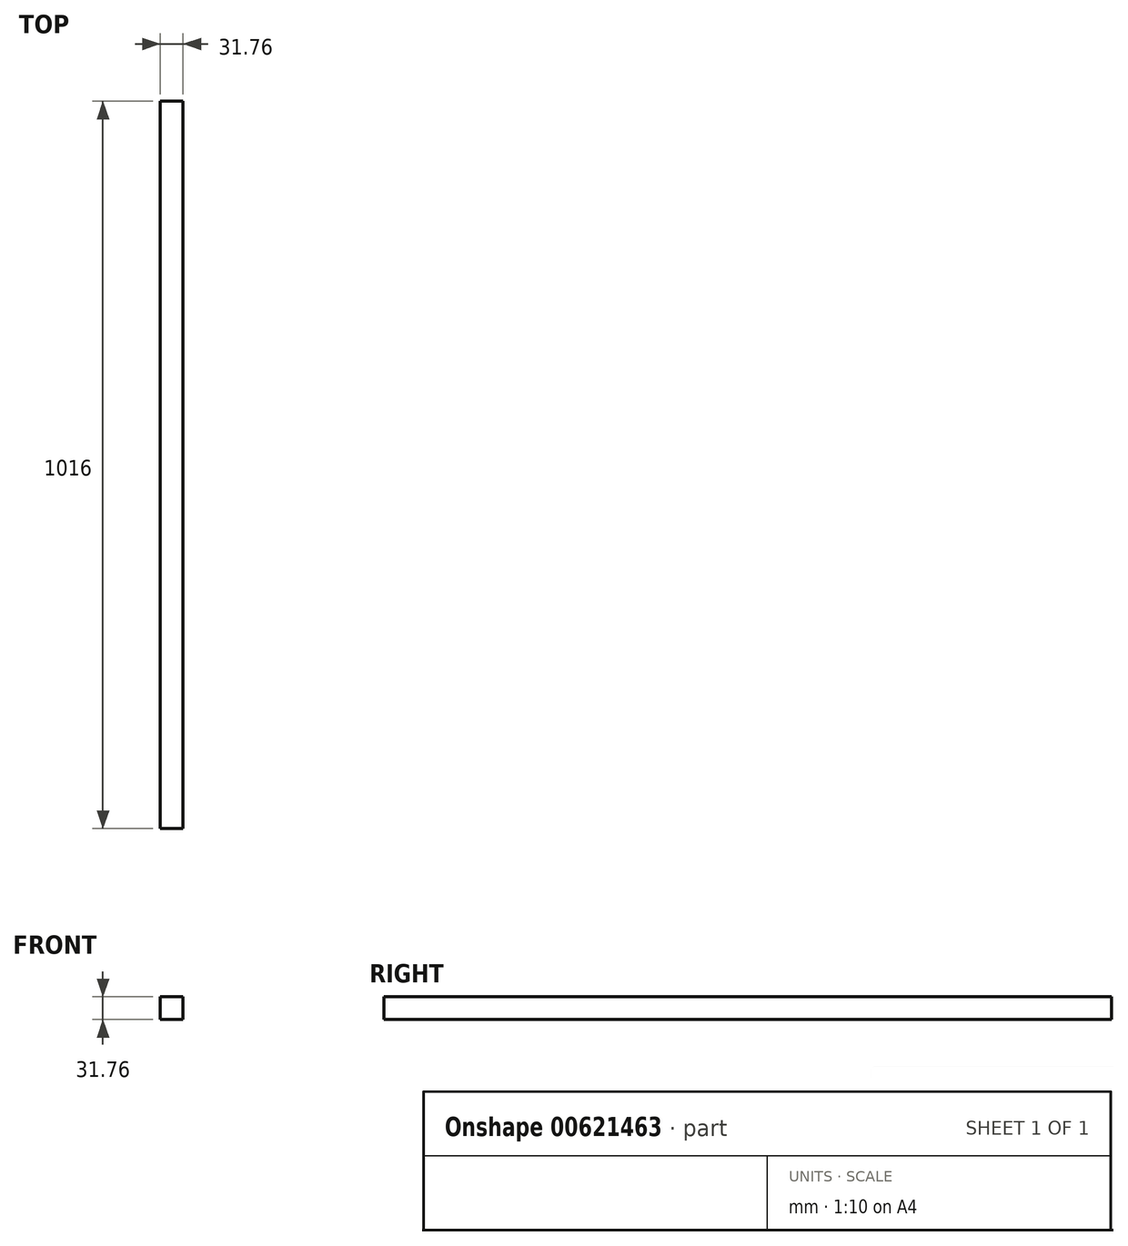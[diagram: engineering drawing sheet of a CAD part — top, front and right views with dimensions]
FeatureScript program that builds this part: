
annotation { "Feature Type Name" : "Feature", "Feature Type Description" : "" }
export const myFeature = defineFeature(function(context is Context, id is Id, definition is map)
    precondition{}
    {
        {
            var Q0;
            Q0=qCreatedBy(makeId("Front.planeOp"),FACE);
            var sketch = newSketch(context, id + "F0", { "sketchPlane" : qUnion([Q0])});
            skLineSegment(sketch, "E0.bottom", {"start": v(15.88, 15.88) * mm, "end": v(-15.88, 15.88) * mm});
            skLineSegment(sketch, "E0.top", {"start": v(15.88, -15.88) * mm, "end": v(-15.88, -15.88) * mm});
            skLineSegment(sketch, "E0.left", {"start": v(15.88, 15.88) * mm, "end": v(15.88, -15.88) * mm});
            skLineSegment(sketch, "E0.right", {"start": v(-15.88, 15.88) * mm, "end": v(-15.88, -15.88) * mm});
            skPoint(sketch, "E0.middle", {"position": v(0, 0) * mm});
            skSolve(sketch);
        }
        {
            var Q0;
            Q0 = qSketchRegion(id + "F0", true);
            extrude(context, id + "F1", {"entities" : qUnion([Q0]), "depth" : 1016 * mm, "offsetDistance" : 25.4 * mm});
        }
    });
